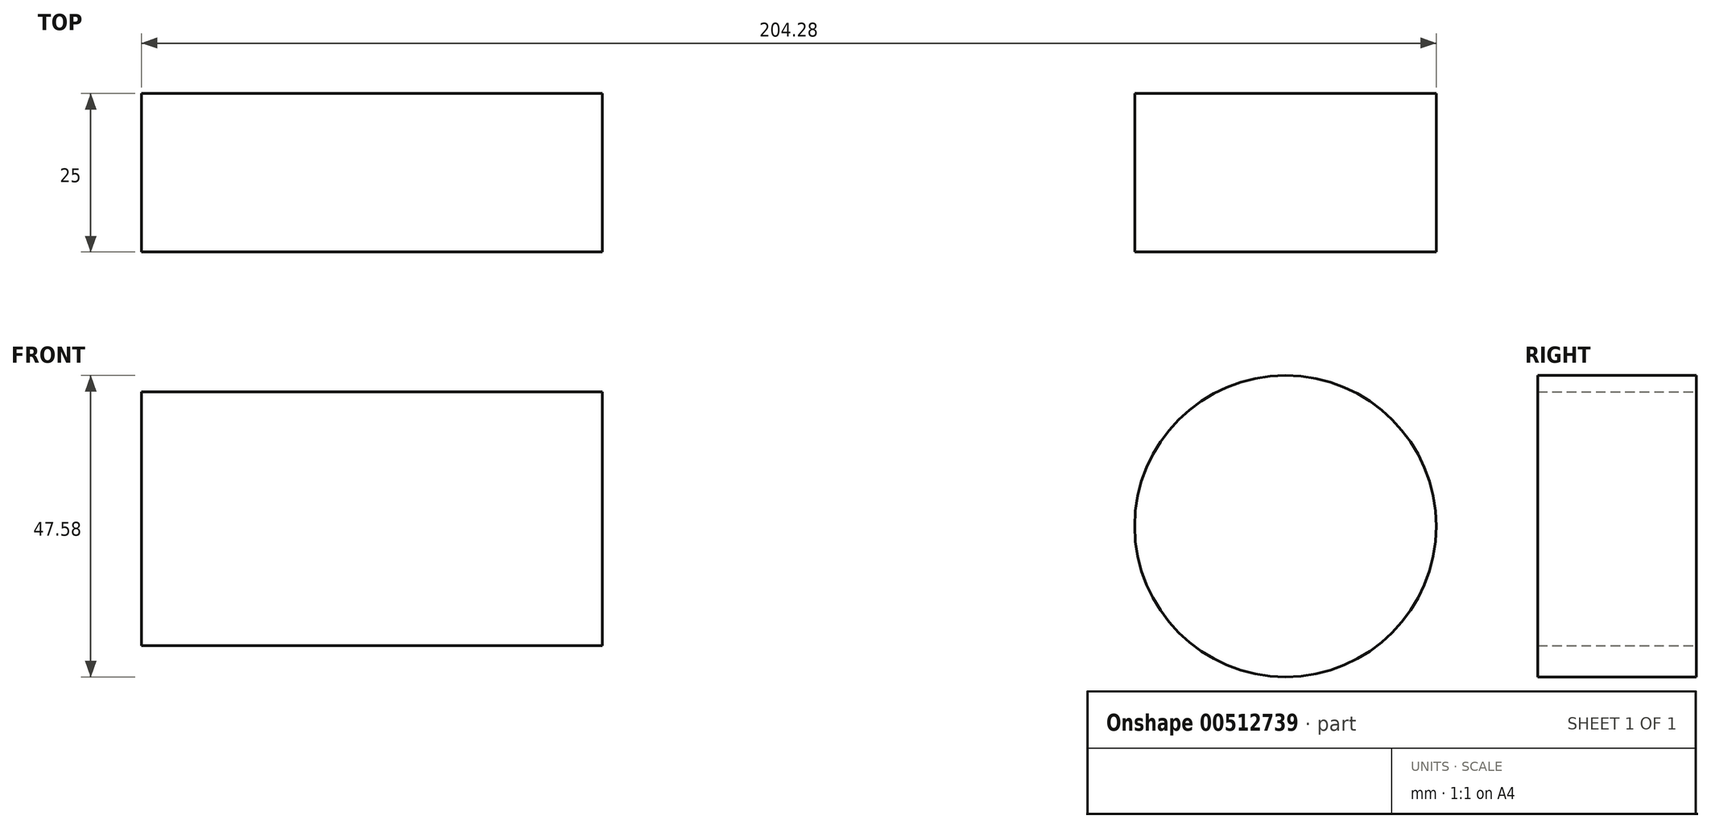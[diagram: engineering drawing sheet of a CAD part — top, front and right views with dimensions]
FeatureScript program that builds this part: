
annotation { "Feature Type Name" : "Feature", "Feature Type Description" : "" }
export const myFeature = defineFeature(function(context is Context, id is Id, definition is map)
    precondition{}
    {
        {
            var Q0;
            Q0=qCreatedBy(makeId("Front.planeOp"),FACE);
            var sketch = newSketch(context, id + "F0", { "sketchPlane" : qUnion([Q0])});
            skLineSegment(sketch, "E0.bottom", {"start": v(-140, 59.1) * mm, "end": v(-67.3, 59.1) * mm});
            skLineSegment(sketch, "E0.top", {"start": v(-140, 19.07) * mm, "end": v(-67.3, 19.07) * mm});
            skLineSegment(sketch, "E0.left", {"start": v(-140, 59.1) * mm, "end": v(-140, 19.07) * mm});
            skLineSegment(sketch, "E0.right", {"start": v(-67.3, 59.1) * mm, "end": v(-67.3, 19.07) * mm});
            skCircle(sketch, "E1", {"center": v(40.49, 37.92) * mm, "radius": 23.8 * mm});
            skSolve(sketch);
        }
        {
            var Q0;
            Q0 = qSketchRegion(id + "F0", true);
            extrude(context, id + "F1", {"entities" : qUnion([Q0]), "depth" : 25 * mm});
        }
    });
